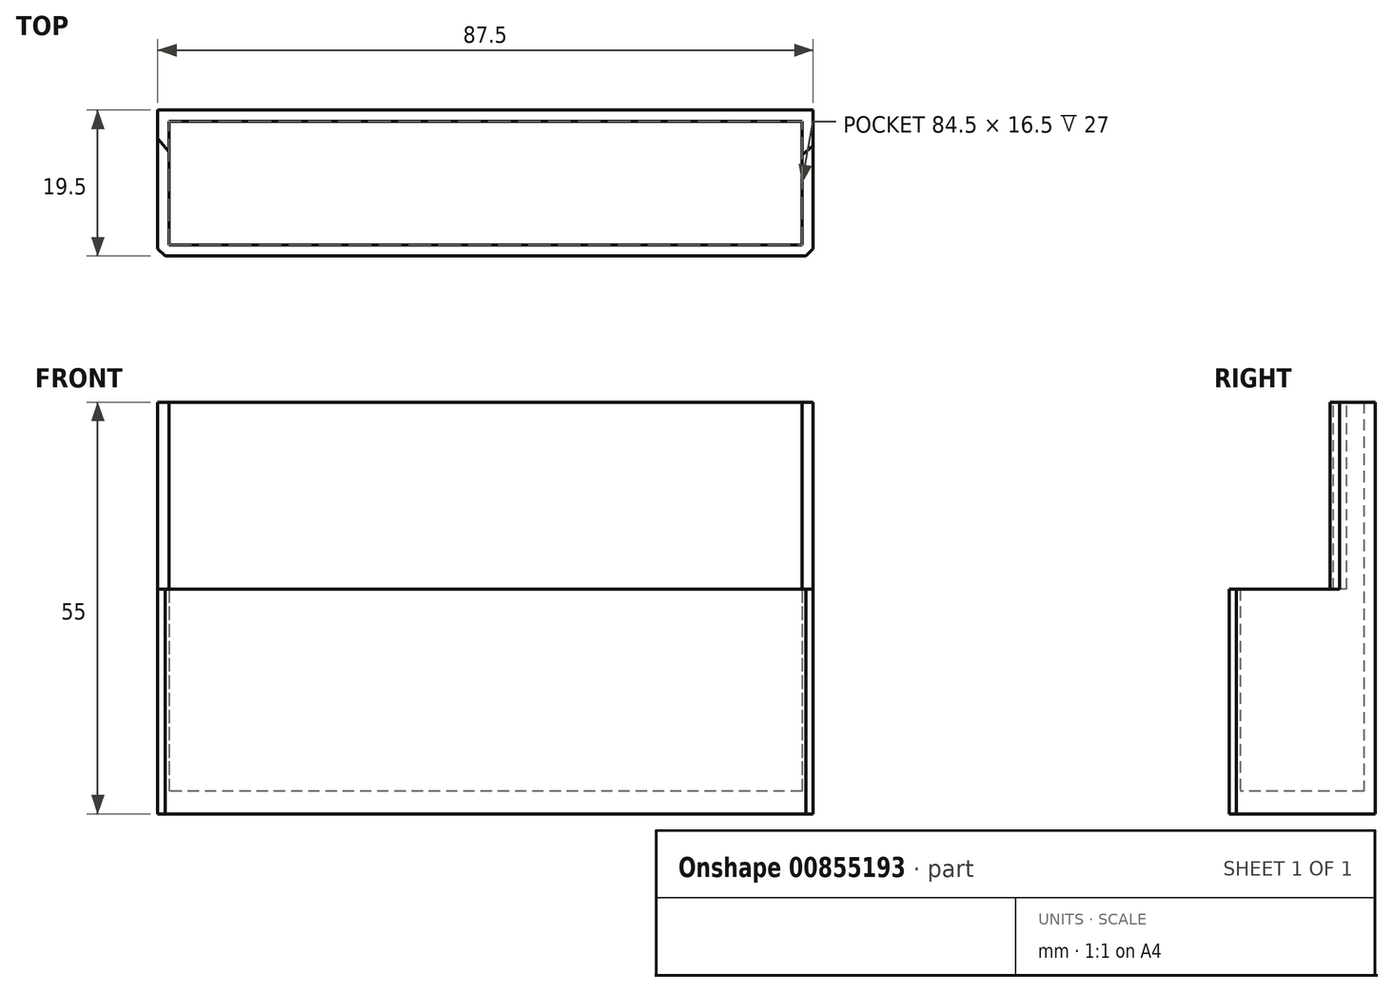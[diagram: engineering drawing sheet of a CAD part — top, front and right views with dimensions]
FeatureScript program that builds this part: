
annotation { "Feature Type Name" : "Feature", "Feature Type Description" : "" }
export const myFeature = defineFeature(function(context is Context, id is Id, definition is map)
    precondition{}
    {
        {
            var Q0;
            Q0=qCreatedBy(makeId("Top.planeOp"),FACE);
            var sketch = newSketch(context, id + "F0", { "sketchPlane" : qUnion([Q0])});
            skLineSegment(sketch, "E0.bottom", {"start": v(42.25, 8.25) * mm, "end": v(-42.25, 8.25) * mm});
            skLineSegment(sketch, "E0.top", {"start": v(42.25, -8.25) * mm, "end": v(-42.25, -8.25) * mm});
            skLineSegment(sketch, "E0.left", {"start": v(42.25, 8.25) * mm, "end": v(42.25, -8.25) * mm});
            skLineSegment(sketch, "E0.right", {"start": v(-42.25, 8.25) * mm, "end": v(-42.25, -8.25) * mm});
            skPoint(sketch, "E0.middle", {"position": v(0, 0) * mm});
            skLineSegment(sketch, "E1.bottom", {"start": v(43.75, 9.75) * mm, "end": v(-43.75, 9.75) * mm});
            skLineSegment(sketch, "E1.top", {"start": v(43.75, -9.75) * mm, "end": v(-43.75, -9.75) * mm});
            skLineSegment(sketch, "E1.left", {"start": v(43.75, 9.75) * mm, "end": v(43.75, -9.75) * mm});
            skLineSegment(sketch, "E1.right", {"start": v(-43.75, 9.75) * mm, "end": v(-43.75, -9.75) * mm});
            skSolve(sketch);
        }
        {
            var Q0;
            Q0=makeQuery(id+"F0.imprint","IMPRINT",FACE,{"disambiguationData":[TD([[makeQuery(id+"F0.imprint","IMPRINT",EDGE,{"derivedFrom":sQuery(id+"F0.wireOp",EDGE,"E0.bottom")}),-1.0]])]});
            extrude(context, id + "F1", {"entities" : qUnion([Q0]), "depth" : 30 * mm, "offsetDistance" : 25 * mm});
        }
        {
            var Q0;
            Q0=makeQuery(id+"F0.imprint","IMPRINT",FACE,{"disambiguationData":[TD([[makeQuery(id+"F0.imprint","IMPRINT",EDGE,{"derivedFrom":sQuery(id+"F0.wireOp",EDGE,"E0.bottom")}),1.0]])]});
            extrude(context, id + "F2", {"entities" : qUnion([Q0]), "operationType" : NewBodyOperationType.ADD, "depth" : 3 * mm, "offsetDistance" : 25 * mm});
        }
        {
            var Q0;
            Q0=makeQuery(id+"F1.opExtrude","SWEPT_EDGE",EDGE,{"disambiguationData":[OSD([sQuery(id+"F0.wireOp",EDGE,"E1.top"),sQuery(id+"F0.wireOp",EDGE,"E1.right")])]});
            var Q1;
            Q1=makeQuery(id+"F1.opExtrude","SWEPT_EDGE",EDGE,{"disambiguationData":[OSD([sQuery(id+"F0.wireOp",EDGE,"E1.top"),sQuery(id+"F0.wireOp",EDGE,"E1.left")])]});
            chamfer(context, id + "F3", {"entities" : qUnion([Q0, Q1]), "width" : 1 * mm, "tangentPropagation" : true});
        }
        {
            var Q0;
            Q0=makeQuery(id+"F1.opExtrude","CAP_FACE",FACE,{"disambiguationData":[OSD([sQuery(id+"F0.wireOp",EDGE,"E0.bottom"),sQuery(id+"F0.wireOp",EDGE,"E0.top"),sQuery(id+"F0.wireOp",EDGE,"E0.left"),sQuery(id+"F0.wireOp",EDGE,"E0.right"),sQuery(id+"F0.wireOp",EDGE,"E1.bottom"),sQuery(id+"F0.wireOp",EDGE,"E1.top"),sQuery(id+"F0.wireOp",EDGE,"E1.left"),sQuery(id+"F0.wireOp",EDGE,"E1.right")])],"isStart":false});
            var sketch = newSketch(context, id + "F4", { "sketchPlane" : qUnion([Q0])});
            skLineSegment(sketch, "E2", {"start": v(-45.67, 0) * mm, "end": v(50, 0) * mm});
            skLineSegment(sketch, "E3", {"start": v(50, 0) * mm, "end": v(42.25, -19.07) * mm});
            skLineSegment(sketch, "E4", {"start": v(42.25, -19.07) * mm, "end": v(-42.25, -20.24) * mm});
            skLineSegment(sketch, "E5", {"start": v(-42.25, -20.24) * mm, "end": v(-48.2, -2.83) * mm});
            skLineSegment(sketch, "E6", {"start": v(-48.2, -2.83) * mm, "end": v(-45.67, 0) * mm});
            skSolve(sketch);
        }
        {
            var Q0;
            {var subQ3=sQuery(id+"F0.wireOp",EDGE,"E0.bottom");Q0=makeQuery(id+"F4.imprint","IMPRINT",FACE,{"disambiguationData":[TD([[makeQuery(id+"F4.imprint","IMPRINT",EDGE,{"derivedFrom":makeQuery(id+"F1.opExtrude","CAP_EDGE",EDGE,{"disambiguationData":[OSD([subQ3])],"isStart":false})}),-1.0]])]});}
            extrude(context, id + "F5", {"entities" : qUnion([Q0]), "operationType" : NewBodyOperationType.ADD, "depth" : 25 * mm, "offsetDistance" : 25 * mm});
        }
        {
            var Q0;
            Q0 = qSketchRegion(id + "F4", true);
            extrude(context, id + "F6", {"entities" : qUnion([Q0]), "operationType" : NewBodyOperationType.REMOVE, "depth" : 25 * mm, "offsetDistance" : 25 * mm});
        }
        {
            var Q0;
            Q0=makeQuery(id+"F5.opExtrude","SWEPT_EDGE",EDGE,{"disambiguationData":[OSD([sQuery(id+"F0.wireOp",EDGE,"E1.right"),sQuery(id+"F4.wireOp",EDGE,"E2")])]});
            var Q1;
            Q1=makeQuery(id+"F5.opExtrude","SWEPT_EDGE",EDGE,{"disambiguationData":[OSD([sQuery(id+"F0.wireOp",EDGE,"E1.left"),sQuery(id+"F4.wireOp",EDGE,"E2")])]});
            chamfer(context, id + "F7", {"entities" : qUnion([Q0, Q1]), "chamferType" : ChamferType.OFFSET_ANGLE, "width" : 5 * mm, "oppositeDirection" : false, "angle" : 50 * degree, "tangentPropagation" : true});
        }
    });
